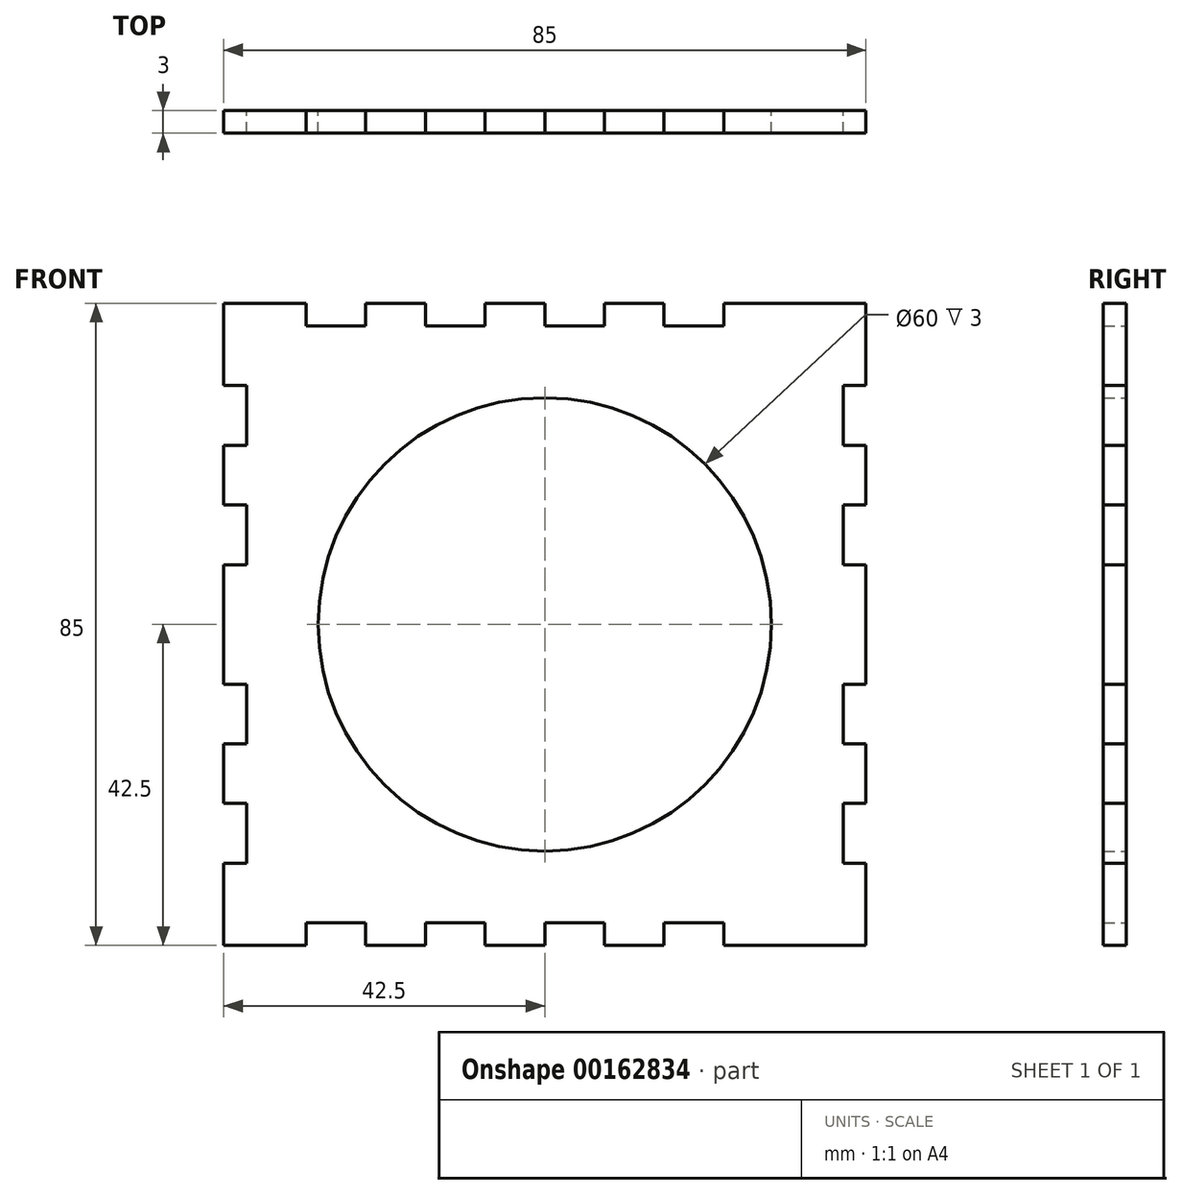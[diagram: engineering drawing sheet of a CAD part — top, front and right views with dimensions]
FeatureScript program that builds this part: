
annotation { "Feature Type Name" : "Feature", "Feature Type Description" : "" }
export const myFeature = defineFeature(function(context is Context, id is Id, definition is map)
    precondition{}
    {
        {
            var Q0;
            Q0=qCreatedBy(makeId("Front.planeOp"),FACE);
            var sketch = newSketch(context, id + "F0", { "sketchPlane" : qUnion([Q0])});
            skLineSegment(sketch, "E0.top", {"start": v(-42.5, -42.5) * mm, "end": v(-31.6, -42.5) * mm});
            skArc(sketch, "E1", {"start": v(0, 30) * mm, "mid": v(-30, 0) * mm, "end": v(0, -30) * mm});
            skLineSegment(sketch, "E2", {"start": v(-42.5, 0) * mm, "end": v(-39.5, 0) * mm});
            skLineSegment(sketch, "E3", {"start": v(-39.5, -7.9) * mm, "end": v(-42.5, -7.9) * mm});
            skLineSegment(sketch, "E4", {"start": v(-42.5, -15.8) * mm, "end": v(-39.5, -15.8) * mm});
            skLineSegment(sketch, "E5", {"start": v(-42.5, -23.7) * mm, "end": v(-39.5, -23.7) * mm});
            skLineSegment(sketch, "E6", {"start": v(-42.5, -31.6) * mm, "end": v(-39.5, -31.6) * mm});
            skLineSegment(sketch, "E7.trimOffspring", {"start": v(-42.5, 0) * mm, "end": v(-42.5, -7.9) * mm});
            skLineSegment(sketch, "E8.trimOffspring", {"start": v(-42.5, -15.8) * mm, "end": v(-42.5, -23.7) * mm});
            skLineSegment(sketch, "E9.trimOffspring", {"start": v(-42.5, -31.6) * mm, "end": v(-42.5, -42.5) * mm});
            skPoint(sketch, "E0.right.start.orphan", {"position": v(42.5, 42.5) * mm});
            skPoint(sketch, "E10.orphan", {"position": v(42.5, -42.5) * mm});
            skLineSegment(sketch, "E11.MirrorCS", {"start": v(42.5, -31.6) * mm, "end": v(39.5, -31.6) * mm});
            skLineSegment(sketch, "E12.MirrorCS", {"start": v(39.5, -7.9) * mm, "end": v(42.5, -7.9) * mm});
            skLineSegment(sketch, "E13.MirrorCS", {"start": v(42.5, 0) * mm, "end": v(39.5, 0) * mm});
            skLineSegment(sketch, "E14.MirrorCS", {"start": v(42.5, -15.8) * mm, "end": v(39.5, -15.8) * mm});
            skLineSegment(sketch, "E15.MirrorCS", {"start": v(42.5, -23.7) * mm, "end": v(39.5, -23.7) * mm});
            skLineSegment(sketch, "E16.MirrorCS", {"start": v(42.5, -31.6) * mm, "end": v(42.5, -42.5) * mm});
            skLineSegment(sketch, "E17.MirrorCS", {"start": v(42.5, -15.8) * mm, "end": v(42.5, -23.7) * mm});
            skLineSegment(sketch, "E18.MirrorCS", {"start": v(42.5, 0) * mm, "end": v(42.5, -7.9) * mm});
            skLineSegment(sketch, "E19.MirrorCS", {"start": v(42.5, -42.5) * mm, "end": v(23.7, -42.5) * mm});
            skArc(sketch, "E20.MirrorCS", {"start": v(0, 30) * mm, "mid": v(30, 0) * mm, "end": v(0, -30) * mm});
            skLineSegment(sketch, "E21.trimOffspring", {"start": v(-39.5, -7.9) * mm, "end": v(-39.5, -15.8) * mm});
            skLineSegment(sketch, "E22.trimOffspring", {"start": v(-39.5, -23.7) * mm, "end": v(-39.5, -31.6) * mm});
            skLineSegment(sketch, "E23.trimOffspring", {"start": v(39.5, -23.7) * mm, "end": v(39.5, -31.6) * mm});
            skLineSegment(sketch, "E24.trimOffspring", {"start": v(39.5, -7.9) * mm, "end": v(39.5, -15.8) * mm});
            skLineSegment(sketch, "E25", {"start": v(-31.6, -39.5) * mm, "end": v(-31.6, -42.5) * mm});
            skLineSegment(sketch, "E26", {"start": v(-23.7, -39.5) * mm, "end": v(-23.7, -42.5) * mm});
            skLineSegment(sketch, "E27", {"start": v(-15.8, -39.5) * mm, "end": v(-15.8, -42.5) * mm});
            skLineSegment(sketch, "E28", {"start": v(-7.9, -39.5) * mm, "end": v(-7.9, -42.5) * mm});
            skLineSegment(sketch, "E29", {"start": v(0, -39.5) * mm, "end": v(0, -42.5) * mm});
            skLineSegment(sketch, "E30", {"start": v(7.9, -39.5) * mm, "end": v(7.9, -42.5) * mm});
            skLineSegment(sketch, "E31", {"start": v(15.8, -39.5) * mm, "end": v(15.8, -42.5) * mm});
            skLineSegment(sketch, "E32", {"start": v(23.7, -39.5) * mm, "end": v(23.7, -42.5) * mm});
            skLineSegment(sketch, "E33.trimOffspring", {"start": v(-23.7, -42.5) * mm, "end": v(-15.8, -42.5) * mm});
            skLineSegment(sketch, "E34.trimOffspring", {"start": v(-7.9, -42.5) * mm, "end": v(0, -42.5) * mm});
            skPoint(sketch, "E35.orphan", {"position": v(0, -42.5) * mm});
            skLineSegment(sketch, "E36.trimOffspring", {"start": v(15.8, -42.5) * mm, "end": v(7.9, -42.5) * mm});
            skPoint(sketch, "E37.end.orphan", {"position": v(31.6, -42.5) * mm});
            skPoint(sketch, "E37.start.orphan", {"position": v(31.6, -39.5) * mm});
            skLineSegment(sketch, "E38.trimOffspring", {"start": v(23.7, -39.5) * mm, "end": v(15.8, -39.5) * mm});
            skPoint(sketch, "E39.orphan", {"position": v(39.5, -39.5) * mm});
            skPoint(sketch, "E40.orphan", {"position": v(-39.5, -39.5) * mm});
            skPoint(sketch, "E41.MirrorCS.end.orphan", {"position": v(39.5, 7.9) * mm});
            skPoint(sketch, "E42.MirrorCS.end.orphan", {"position": v(42.5, 7.9) * mm});
            skPoint(sketch, "E43.MirrorCS.start.orphan", {"position": v(42.5, 15.8) * mm});
            skPoint(sketch, "E44.trimOffspring.end.orphan", {"position": v(39.5, 15.8) * mm});
            skPoint(sketch, "E45.MirrorCS.end.orphan", {"position": v(39.5, 23.7) * mm});
            skPoint(sketch, "E46.MirrorCS.end.orphan", {"position": v(42.5, 23.7) * mm});
            skPoint(sketch, "E47.MirrorCS.end.orphan", {"position": v(42.5, 31.6) * mm});
            skPoint(sketch, "E47.MirrorCS.start.orphan", {"position": v(39.5, 31.6) * mm});
            skPoint(sketch, "E48.MirrorCS.end.orphan", {"position": v(0, 39.5) * mm});
            skPoint(sketch, "E49.MirrorCS.end.orphan", {"position": v(0, 42.5) * mm});
            skPoint(sketch, "E50.MirrorCS.end.orphan", {"position": v(42.5, 39.5) * mm});
            skPoint(sketch, "E50.MirrorCS.start.orphan", {"position": v(39.5, 39.5) * mm});
            skPoint(sketch, "E0.left.start.orphan", {"position": v(-42.5, 42.5) * mm});
            skPoint(sketch, "E51.end.orphan", {"position": v(-42.5, 39.5) * mm});
            skPoint(sketch, "E52.left.start.orphan", {"position": v(-39.5, 39.5) * mm});
            skPoint(sketch, "E53.start.orphan", {"position": v(-39.5, 31.6) * mm});
            skPoint(sketch, "E54.trimOffspring.start.orphan", {"position": v(-42.5, 31.6) * mm});
            skPoint(sketch, "E55.start.orphan", {"position": v(-42.5, 23.7) * mm});
            skPoint(sketch, "E56.trimOffspring.start.orphan", {"position": v(-39.5, 23.7) * mm});
            skPoint(sketch, "E57.end.orphan", {"position": v(-39.5, 15.8) * mm});
            skPoint(sketch, "E58.trimOffspring.start.orphan", {"position": v(-42.5, 15.8) * mm});
            skPoint(sketch, "E59.start.orphan", {"position": v(-42.5, 7.9) * mm});
            skPoint(sketch, "E60.trimOffspring.start.orphan", {"position": v(-39.5, 7.9) * mm});
            skLineSegment(sketch, "E61.MirrorCS", {"start": v(0, 39.5) * mm, "end": v(0, 42.5) * mm});
            skLineSegment(sketch, "E62.MirrorCS", {"start": v(23.7, 39.5) * mm, "end": v(23.7, 42.5) * mm});
            skLineSegment(sketch, "E63.MirrorCS", {"start": v(-31.6, 39.5) * mm, "end": v(-31.6, 42.5) * mm});
            skLineSegment(sketch, "E64.MirrorCS", {"start": v(15.8, 39.5) * mm, "end": v(15.8, 42.5) * mm});
            skLineSegment(sketch, "E65.MirrorCS", {"start": v(-15.8, 39.5) * mm, "end": v(-15.8, 42.5) * mm});
            skLineSegment(sketch, "E66.MirrorCS", {"start": v(42.5, 23.7) * mm, "end": v(39.5, 23.7) * mm});
            skLineSegment(sketch, "E67.MirrorCS", {"start": v(-23.7, 39.5) * mm, "end": v(-23.7, 42.5) * mm});
            skLineSegment(sketch, "E68.MirrorCS", {"start": v(42.5, 31.6) * mm, "end": v(39.5, 31.6) * mm});
            skLineSegment(sketch, "E69.MirrorCS", {"start": v(39.5, 7.9) * mm, "end": v(42.5, 7.9) * mm});
            skLineSegment(sketch, "E70.MirrorCS", {"start": v(7.9, 39.5) * mm, "end": v(7.9, 42.5) * mm});
            skLineSegment(sketch, "E71.MirrorCS", {"start": v(-7.9, 39.5) * mm, "end": v(-7.9, 42.5) * mm});
            skLineSegment(sketch, "E72.MirrorCS", {"start": v(42.5, 15.8) * mm, "end": v(39.5, 15.8) * mm});
            skLineSegment(sketch, "E73.MirrorCS", {"start": v(-42.5, 31.6) * mm, "end": v(-39.5, 31.6) * mm});
            skLineSegment(sketch, "E74.MirrorCS", {"start": v(-42.5, 23.7) * mm, "end": v(-39.5, 23.7) * mm});
            skLineSegment(sketch, "E75.MirrorCS", {"start": v(-42.5, 15.8) * mm, "end": v(-39.5, 15.8) * mm});
            skLineSegment(sketch, "E76.MirrorCS", {"start": v(-39.5, 7.9) * mm, "end": v(-42.5, 7.9) * mm});
            skLineSegment(sketch, "E77.MirrorCS", {"start": v(42.5, 15.8) * mm, "end": v(42.5, 23.7) * mm});
            skLineSegment(sketch, "E78.MirrorCS", {"start": v(-39.5, 7.9) * mm, "end": v(-39.5, 15.8) * mm});
            skLineSegment(sketch, "E79.MirrorCS", {"start": v(-23.7, 42.5) * mm, "end": v(-15.8, 42.5) * mm});
            skPoint(sketch, "E80.MirrorP", {"position": v(31.6, 39.5) * mm});
            skLineSegment(sketch, "E81.MirrorCS", {"start": v(42.5, 0) * mm, "end": v(42.5, 7.9) * mm});
            skLineSegment(sketch, "E82.MirrorCS", {"start": v(42.5, 31.6) * mm, "end": v(42.5, 42.5) * mm});
            skLineSegment(sketch, "E83.MirrorCS", {"start": v(23.7, 39.5) * mm, "end": v(15.8, 39.5) * mm});
            skLineSegment(sketch, "E84.MirrorCS", {"start": v(15.8, 42.5) * mm, "end": v(7.9, 42.5) * mm});
            skLineSegment(sketch, "E85.MirrorCS", {"start": v(39.5, 23.7) * mm, "end": v(39.5, 31.6) * mm});
            skLineSegment(sketch, "E86.MirrorCS", {"start": v(-39.5, 23.7) * mm, "end": v(-39.5, 31.6) * mm});
            skPoint(sketch, "E87.MirrorP", {"position": v(31.6, 42.5) * mm});
            skLineSegment(sketch, "E88.MirrorCS", {"start": v(-42.5, 42.5) * mm, "end": v(-31.6, 42.5) * mm});
            skLineSegment(sketch, "E89.MirrorCS", {"start": v(39.5, 7.9) * mm, "end": v(39.5, 15.8) * mm});
            skLineSegment(sketch, "E90.MirrorCS", {"start": v(-7.9, 42.5) * mm, "end": v(0, 42.5) * mm});
            skLineSegment(sketch, "E91.MirrorCS", {"start": v(42.5, 42.5) * mm, "end": v(23.7, 42.5) * mm});
            skLineSegment(sketch, "E92.MirrorCS", {"start": v(-31.6, 39.5) * mm, "end": v(-23.7, 39.5) * mm});
            skLineSegment(sketch, "E93.MirrorCS", {"start": v(-42.5, 0) * mm, "end": v(-42.5, 7.9) * mm});
            skLineSegment(sketch, "E94.MirrorCS", {"start": v(-42.5, 31.6) * mm, "end": v(-42.5, 42.5) * mm});
            skLineSegment(sketch, "E95.MirrorCS", {"start": v(-42.5, 15.8) * mm, "end": v(-42.5, 23.7) * mm});
            skLineSegment(sketch, "E96.trimOffspring", {"start": v(-15.8, 39.5) * mm, "end": v(-7.9, 39.5) * mm});
            skLineSegment(sketch, "E97.trimOffspring", {"start": v(7.9, 39.5) * mm, "end": v(0, 39.5) * mm});
            skLineSegment(sketch, "E98.trimOffspring", {"start": v(-15.8, -39.5) * mm, "end": v(-7.9, -39.5) * mm});
            skLineSegment(sketch, "E99.trimOffspring", {"start": v(7.9, -39.5) * mm, "end": v(0, -39.5) * mm});
            skPoint(sketch, "E100.MirrorCS.start.orphan", {"position": v(0, 30) * mm});
            skPoint(sketch, "E101.orphan", {"position": v(0, -39.5) * mm});
            skLineSegment(sketch, "E102", {"start": v(-31.6, -39.5) * mm, "end": v(-23.7, -39.5) * mm});
            skSolve(sketch);
        }
        {
            var Q0;
            Q0 = qSketchRegion(id + "F0", true);
            extrude(context, id + "F1", {"entities" : qUnion([Q0]), "depth" : 3 * mm});
        }
    });
